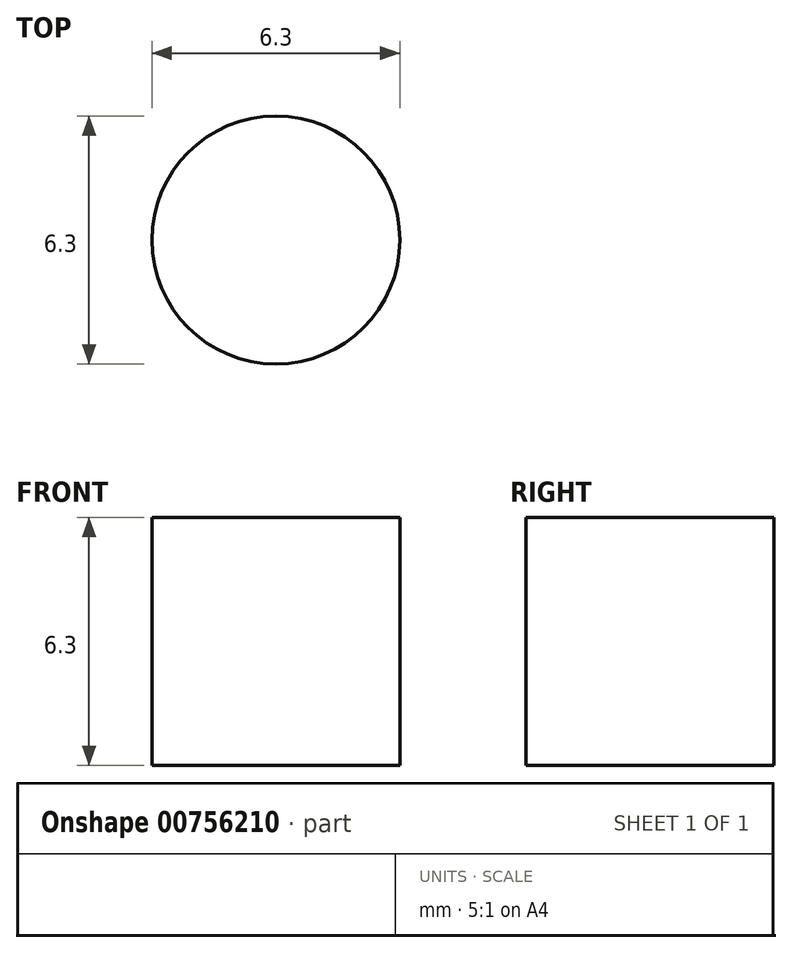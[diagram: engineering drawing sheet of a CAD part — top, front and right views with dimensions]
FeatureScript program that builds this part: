
annotation { "Feature Type Name" : "Feature", "Feature Type Description" : "" }
export const myFeature = defineFeature(function(context is Context, id is Id, definition is map)
    precondition{}
    {
        {
            var Q0;
            Q0=qCreatedBy(makeId("Top.planeOp"),FACE);
            var sketch = newSketch(context, id + "F0", { "sketchPlane" : qUnion([Q0])});
            skCircle(sketch, "E0", {"center": v(0, 0) * mm, "radius": 3.15 * mm});
            skSolve(sketch);
        }
        {
            var Q0;
            Q0=qSketchRegion(id+"F0",true);
            extrude(context, id + "F1", {"entities" : qUnion([Q0]), "endBound" : BoundingType.SYMMETRIC, "depth" : 6.3 * mm, "offsetDistance" : 25 * mm});
        }
    });
